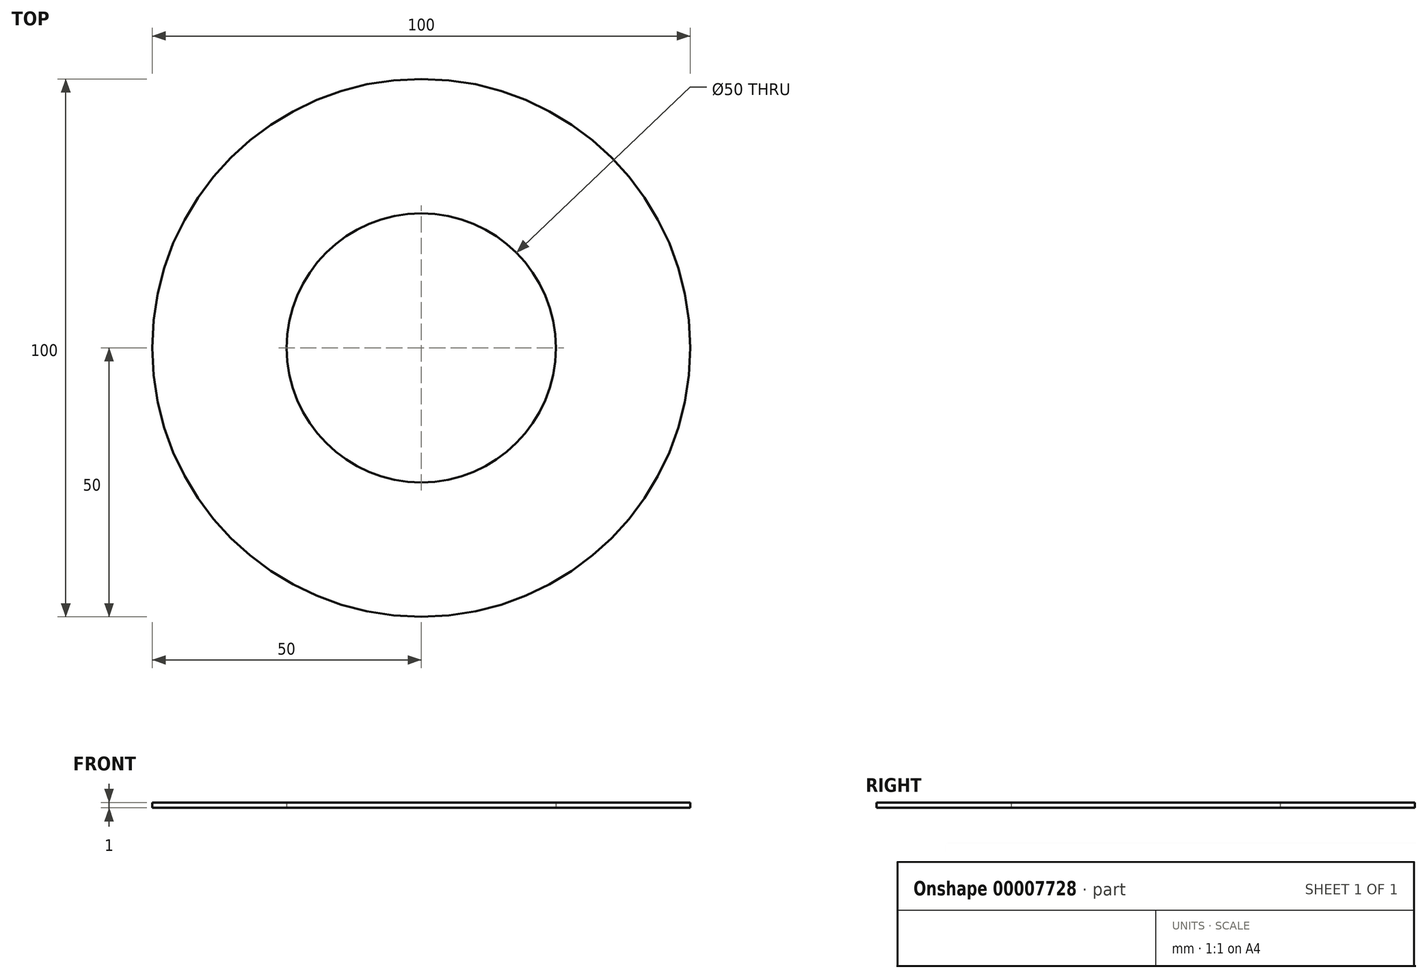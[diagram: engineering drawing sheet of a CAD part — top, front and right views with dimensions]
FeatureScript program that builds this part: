
annotation { "Feature Type Name" : "Feature", "Feature Type Description" : "" }
export const myFeature = defineFeature(function(context is Context, id is Id, definition is map)
    precondition{}
    {
        {
            var Q0;
            Q0=qCreatedBy(makeId("Top.planeOp"),FACE);
            var sketch = newSketch(context, id + "F0", { "sketchPlane" : qUnion([Q0])});
            skCircle(sketch, "E0", {"center": v(0, 0) * mm, "radius": 50 * mm});
            skCircle(sketch, "E1", {"center": v(0, 0) * mm, "radius": 25 * mm});
            skSolve(sketch);
        }
        {
            var Q0;
            Q0=makeQuery(id+"F0.imprint","IMPRINT",FACE,{"disambiguationData":[TD([[makeQuery(id+"F0.imprint","IMPRINT",EDGE,{"derivedFrom":sQuery(id+"F0.wireOp",EDGE,"E0")}),1.0]])]});
            extrude(context, id + "F1", {"entities" : qUnion([Q0]), "depth" : 1 * mm});
        }
    });
